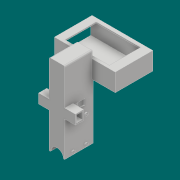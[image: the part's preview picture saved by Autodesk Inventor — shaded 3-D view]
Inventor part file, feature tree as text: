
AUTODESK INVENTOR PART (.ipt)
format: ipt  version: 2017.3 (Build 213257000, 257)  size: 502,272 bytes
history: native  units: mm
features: extrude x30, sketch x29, projected_geometry x14, fillet x2
ambient origin geometry x8: Origin, YZ Plane, XZ Plane, XY Plane, X Axis, Y Axis, Z Axis, Center Point
bodies: Solid1 (feature_tree)
feature tree (75):
  extrude  "Extrusion1"  Depth=45.0mm
  extrude  "Extrusion2"  Depth=2.0mm TaperAngle=0.0deg
  extrude  "Extrusion3"  Depth=6.0mm
  extrude  "Extrusion4"  Depth=12.0mm
  extrude  "Extrusion5"  Depth=18.0mm TaperAngle=0.0deg
  extrude  "Extrusion6"  Depth=18.0mm TaperAngle=0.0deg
  extrude  "Extrusion7"  Depth=10.0mm
  extrude  "Extrusion8"  Depth=5.0mm
  extrude  "Extrusion9"  Depth=5.0mm
  extrude  "Extrusion10"  Depth=5.0mm TaperAngle=0.0deg
  extrude  "Extrusion11"  Depth=1.0mm
  extrude  "Extrusion12"  Depth=1.0mm TaperAngle=0.0deg
  extrude  "Extrusion13"  Depth=47.25mm TaperAngle=0.0deg
  extrude  "Extrusion14"  Depth=1.0mm
  extrude  "Extrusion15"  Depth=1.0mm
  extrude  "Extrusion16"  Depth=1.0mm
  extrude  "Extrusion17"  Depth=2.0mm
  extrude  "Extrusion18"  Depth=2.0mm
  extrude  "Extrusion19"  Depth=22.0mm
  extrude  "Extrusion20"  Depth=22.0mm
  extrude  "Extrusion21"  Depth=44.0mm
  extrude  "Extrusion22"  Depth=2.0mm
  extrude  "Extrusion24"  Depth=2.0mm
  extrude  "Extrusion25"  Depth=1.0mm
  extrude  "Extrusion26"  Depth=1.0mm
  extrude  "Extrusion27"  Depth=3.0mm TaperAngle=0.0deg
  extrude  "Extrusion28"  Depth=2.5mm
  extrude  "Extrusion29"  Depth=30.0mm
  extrude  "Extrusion30"  Depth=2.0mm
  extrude  "Extrusion31"  Depth=1.0mm
  fillet  "Fillet1"  Radius=1.0mm
  fillet  "Fillet2"  Radius=1.0mm
  sketch  "Sketch1"  dims[d0=22.0mm d1=45.0mm]
  sketch  "Sketch2"  dims[d2=2.0mm d3=40.0mm d4=0.0mm]
  sketch  "Sketch3"  dims[d5=2.0mm d6=6.0mm]
  sketch  "Sketch4"  dims[d7=10.0mm d8=12.0mm]
  projected_geometry  "Projected Loop1"
  sketch  "Sketch5"  dims[d9=2.0mm d10=18.0mm d11=0.0mm]
  sketch  "Sketch6"  dims[d12=18.0mm d13=0.0mm d14=40.0mm d15=0.0mm]
  sketch  "Sketch7"  dims[d16=5.0mm d17=10.0mm]
  projected_geometry  "Projected Loop2"
  sketch  "Sketch8"  dims[d18=2.0mm d19=5.0mm]
  sketch  "Sketch9"  dims[d20=20.0mm d21=0.0mm d22=5.0mm]
  projected_geometry  "Projected Loop3"
  sketch  "Sketch10"  dims[d23=5.0mm d24=5.0mm d25=0.0mm]
  projected_geometry  "Projected Loop4"
  sketch  "Sketch11"  dims[d26=30.0mm d27=0.0mm d28=1.0mm]
  projected_geometry  "Projected Loop5"
  sketch  "Sketch12"  dims[d29=70.0mm d30=0.0mm d31=1.0mm d32=0.0mm]
  sketch  "Sketch13"  dims[d33=17.25mm d34=0.0mm d35=47.25mm d36=0.0mm]
  sketch  "Sketch14"  dims[d37=1.0mm d38=21.8mm]
  sketch  "Sketch15"  dims[d39=1.0mm d40=44.3mm]
  projected_geometry  "Projected Loop6"
  projected_geometry  "Projected Loop7"
  sketch  "Sketch17"  dims[d41=1.0mm d42=1.0mm]
  projected_geometry  "Projected Loop8"
  projected_geometry  "Projected Loop9"
  sketch  "Sketch18"  dims[d43=2.0mm d44=2.0mm]
  sketch  "Sketch19"  dims[d45=2.0mm d46=2.0mm]
  sketch  "Sketch20"  dims[d47=2.0mm d48=0.0mm d49=22.0mm]
  sketch  "Sketch21"  dims[d50=44.0mm d51=22.0mm]
  sketch  "Sketch22"  dims[d52=44.0mm d53=44.0mm]
  projected_geometry  "Projected Loop10"
  sketch  "Sketch24"  dims[d54=2.0mm d55=0.0mm d56=3.5mm]
  sketch  "Sketch25"  dims[d57=3.5mm d58=2.0mm]
  sketch  "Sketch26"  dims[d59=1.0mm d60=1.0mm]
  projected_geometry  "Projected Loop11"
  sketch  "Sketch27"  dims[d61=1.0mm d62=1.0mm]
  projected_geometry  "Projected Loop12"
  sketch  "Sketch28"  dims[d63=1.0mm d64=0.0mm d65=3.0mm d66=0.0mm]
  sketch  "Sketch29"  dims[d67=50.0mm d68=2.5mm]
  projected_geometry  "Projected Loop13"
  projected_geometry  "Projected Loop14"
  sketch  "Sketch30"  dims[d69=2.0mm d70=30.0mm]
  sketch  "Sketch31"  dims[d71=16.5mm d72=2.0mm d73=1.0mm d74=1.0mm d75=1.0mm d76=0.0mm d77=3.0mm d78=0.0mm d79=5.0mm d80=2.0mm d81=26.0mm d82=2.0mm d83=30.0mm d84=0.0mm d85=26.0mm d86=2.0mm d87=3.0mm d88=0.0mm d89=10.0mm d90=0.0mm d91=30.0mm d92=100.0mm d93=0.0mm d94=2.0mm d95=0.0mm d98=37.3mm d99=74.6mm d100=3.0mm d101=2.0mm d102=0.0mm d103=13.0mm d104=13.0mm d105=57.5mm d106=2.0mm d107=57.5mm d108=2.0mm d109=2.0mm d110=0.0mm d111=2.0mm d112=0.0mm d113=2.0mm d114=2.0mm d115=0.0mm d116=2.0mm d117=2.0mm d118=0.0mm d119=2.0mm d120=0.0mm d121=2.0mm d122=0.0mm d123=2.0mm d124=0.0mm d125=2.0mm d126=2.0mm]
